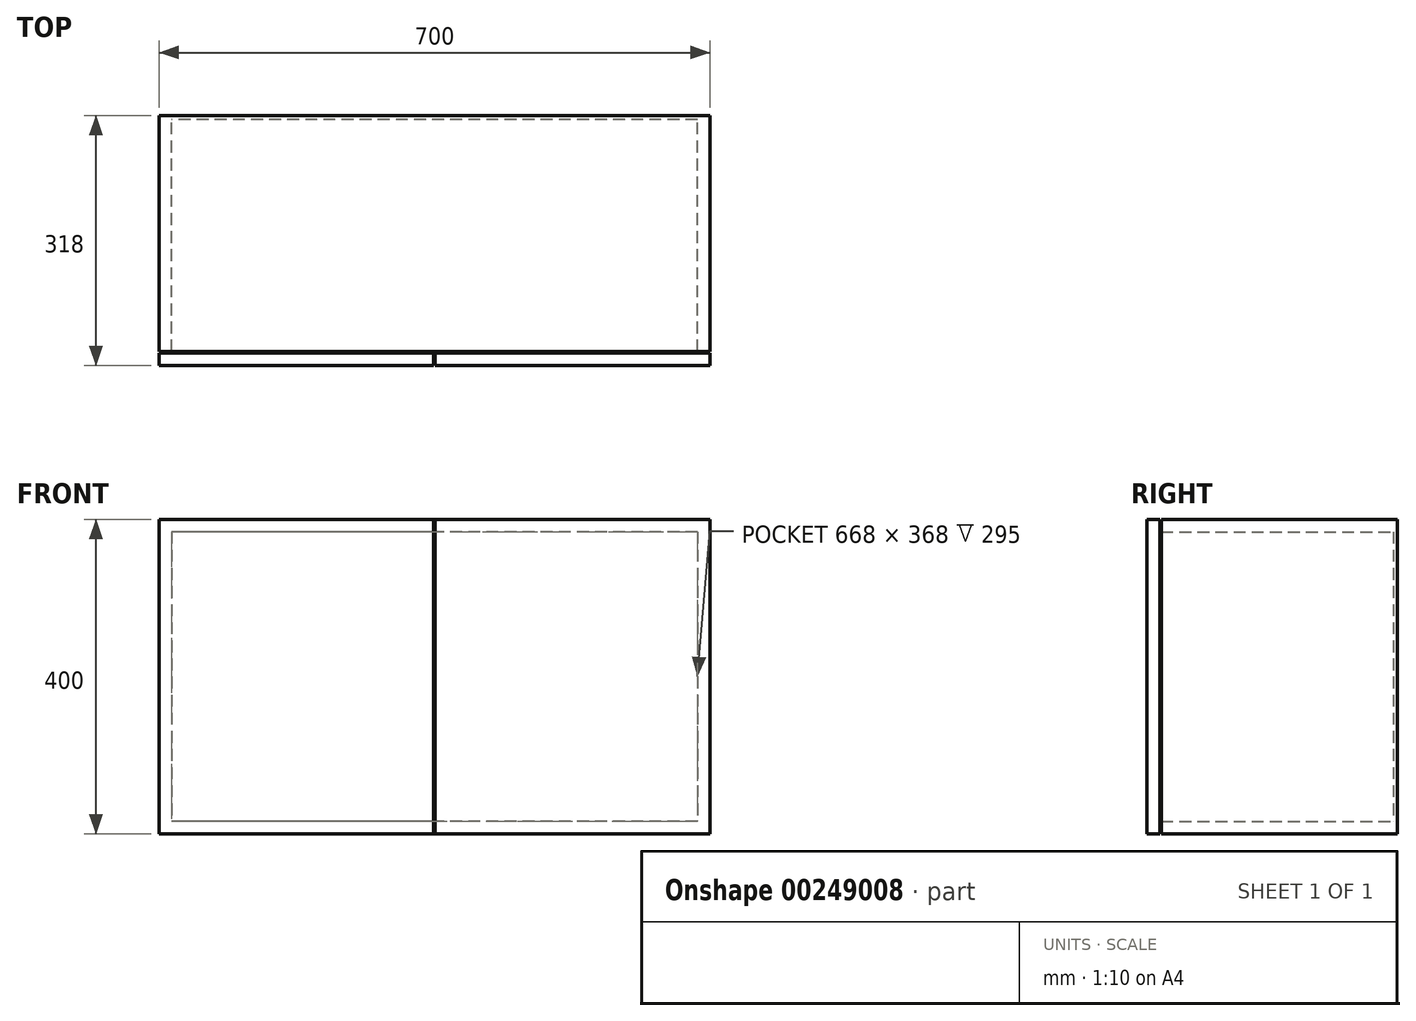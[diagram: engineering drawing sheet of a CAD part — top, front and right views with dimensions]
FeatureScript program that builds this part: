
annotation { "Feature Type Name" : "Feature", "Feature Type Description" : "" }
export const myFeature = defineFeature(function(context is Context, id is Id, definition is map)
    precondition{}
    {
        {
            var Q0;
            Q0=qCreatedBy(makeId("Front.planeOp"),FACE);
            var sketch = newSketch(context, id + "F0", { "sketchPlane" : qUnion([Q0])});
            skLineSegment(sketch, "E0.bottom", {"start": v(350, 200) * mm, "end": v(-350, 200) * mm});
            skLineSegment(sketch, "E0.top", {"start": v(350, -200) * mm, "end": v(-350, -200) * mm});
            skLineSegment(sketch, "E0.left", {"start": v(350, 200) * mm, "end": v(350, -200) * mm});
            skLineSegment(sketch, "E0.right", {"start": v(-350, 200) * mm, "end": v(-350, -200) * mm});
            skPoint(sketch, "E0.middle", {"position": v(0, 0) * mm});
            skSolve(sketch);
        }
        {
            var Q0;
            Q0=makeQuery(id+"F0.imprint","IMPRINT",FACE,{"disambiguationData":[TD([[makeQuery(id+"F0.imprint","IMPRINT",EDGE,{"derivedFrom":sQuery(id+"F0.wireOp",EDGE,"E0.bottom")}),1.0]])]});
            extrude(context, id + "F1", {"entities" : qUnion([Q0]), "depth" : 300 * mm});
        }
        {
            var Q0;
            Q0=makeQuery(id+"F1.opExtrude","CAP_FACE",FACE,{"disambiguationData":[OSD([sQuery(id+"F0.wireOp",EDGE,"E0.bottom"),sQuery(id+"F0.wireOp",EDGE,"E0.top"),sQuery(id+"F0.wireOp",EDGE,"E0.left"),sQuery(id+"F0.wireOp",EDGE,"E0.right")])],"isStart":false});
            shell(context, id + "F2", {"entities" : qUnion([Q0]), "thickness" : 16 * mm});
        }
        {
            var Q0;
            Q0=makeQuery(id+"F2.opShell","OFFSET_FACE",FACE,{"disambiguationData":[OSD([sQuery(id+"F0.wireOp",EDGE,"E0.bottom"),sQuery(id+"F0.wireOp",EDGE,"E0.top"),sQuery(id+"F0.wireOp",EDGE,"E0.left"),sQuery(id+"F0.wireOp",EDGE,"E0.right")])]});
            extrude(context, id + "F3", {"entities" : qUnion([Q0]), "operationType" : NewBodyOperationType.REMOVE, "oppositeDirection" : true, "depth" : (16 - 5) * mm});
        }
        {
            var Q0;
            Q0=makeQuery(id+"F1.opExtrude","CAP_FACE",FACE,{"disambiguationData":[OSD([sQuery(id+"F0.wireOp",EDGE,"E0.bottom"),sQuery(id+"F0.wireOp",EDGE,"E0.top"),sQuery(id+"F0.wireOp",EDGE,"E0.left"),sQuery(id+"F0.wireOp",EDGE,"E0.right")])],"isStart":false});
            cPlane(context, id + "F4", {"entities" : qUnion([Q0]), "cplaneType" : CPlaneType.OFFSET, "offset" : 2 * mm, "width" : 150 * mm, "height" : 150 * mm});
        }
        {
            var Q0;
            Q0=qCreatedBy(id+"F4.planeOp",FACE);
            var sketch = newSketch(context, id + "F5", { "sketchPlane" : qUnion([Q0])});
            skLineSegment(sketch, "E1.0", {"start": v(350, 200) * mm, "end": v(-350, 200) * mm});
            skLineSegment(sketch, "E2.0", {"start": v(-350, 200) * mm, "end": v(-350, -200) * mm});
            skLineSegment(sketch, "E3.0", {"start": v(350, -200) * mm, "end": v(-350, -200) * mm});
            skLineSegment(sketch, "E4.0", {"start": v(350, 200) * mm, "end": v(350, -200) * mm});
            skSolve(sketch);
        }
        {
            var Q0;
            Q0=qSketchRegion(id+"F5",true);
            extrude(context, id + "F6", {"entities" : qUnion([Q0]), "depth" : 16 * mm});
        }
        {
            var Q0;
            Q0=makeQuery(id+"F6.opExtrude","CAP_FACE",FACE,{"disambiguationData":[OSD([sQuery(id+"F5.wireOp",EDGE,"E1.0"),sQuery(id+"F5.wireOp",EDGE,"E2.0"),sQuery(id+"F5.wireOp",EDGE,"E3.0"),sQuery(id+"F5.wireOp",EDGE,"E4.0")])],"isStart":false});
            var sketch = newSketch(context, id + "F7", { "sketchPlane" : qUnion([Q0])});
            skLineSegment(sketch, "E5.bottom", {"start": v(1, 200) * mm, "end": v(-1, 200) * mm});
            skLineSegment(sketch, "E5.top", {"start": v(1, -200) * mm, "end": v(-1, -200) * mm});
            skLineSegment(sketch, "E5.left", {"start": v(1, 200) * mm, "end": v(1, -200) * mm});
            skLineSegment(sketch, "E5.right", {"start": v(-1, 200) * mm, "end": v(-1, -200) * mm});
            skPoint(sketch, "E5.middle", {"position": v(0, 0) * mm});
            skSolve(sketch);
        }
        {
            var Q0;
            Q0=qSketchRegion(id+"F7",true);
            var Q1;
            Q1=makeQuery(id+"F6.opExtrude","CAP_FACE",FACE,{"disambiguationData":[OSD([sQuery(id+"F5.wireOp",EDGE,"E1.0"),sQuery(id+"F5.wireOp",EDGE,"E2.0"),sQuery(id+"F5.wireOp",EDGE,"E3.0"),sQuery(id+"F5.wireOp",EDGE,"E4.0")])],"isStart":true});
            extrude(context, id + "F8", {"entities" : qUnion([Q0]), "operationType" : NewBodyOperationType.REMOVE, "endBound" : BoundingType.UP_TO_SURFACE, "oppositeDirection" : true, "endBoundEntityFace" : qUnion([Q1]), "depth" : 25 * mm});
        }
    });
